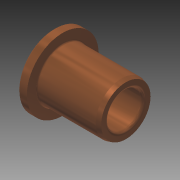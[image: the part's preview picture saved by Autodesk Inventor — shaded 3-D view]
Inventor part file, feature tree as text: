
AUTODESK INVENTOR PART (.ipt)
format: ipt  version: 2012 (Build 160160000, 160)  size: 116,224 bytes
history: native  units: mm (DEFAULTED — no unit token found)
features: revolve x1, sketch x1
ambient origin geometry x8: Origin, YZ Plane, XZ Plane, XY Plane, X Axis, Y Axis, Z Axis, Center Point
bodies: Solid1 (feature_tree)
feature tree (2):
  revolve  "Revolution1"  [1 undecoded]
  sketch  "Sketch_1"  dims[d0=360.0deg]
note: 1 required parameter value undecoded (feature->parameter linkage not recoverable at this tier; creation-order binding heuristic only, values carry confidence <= 0.55)
